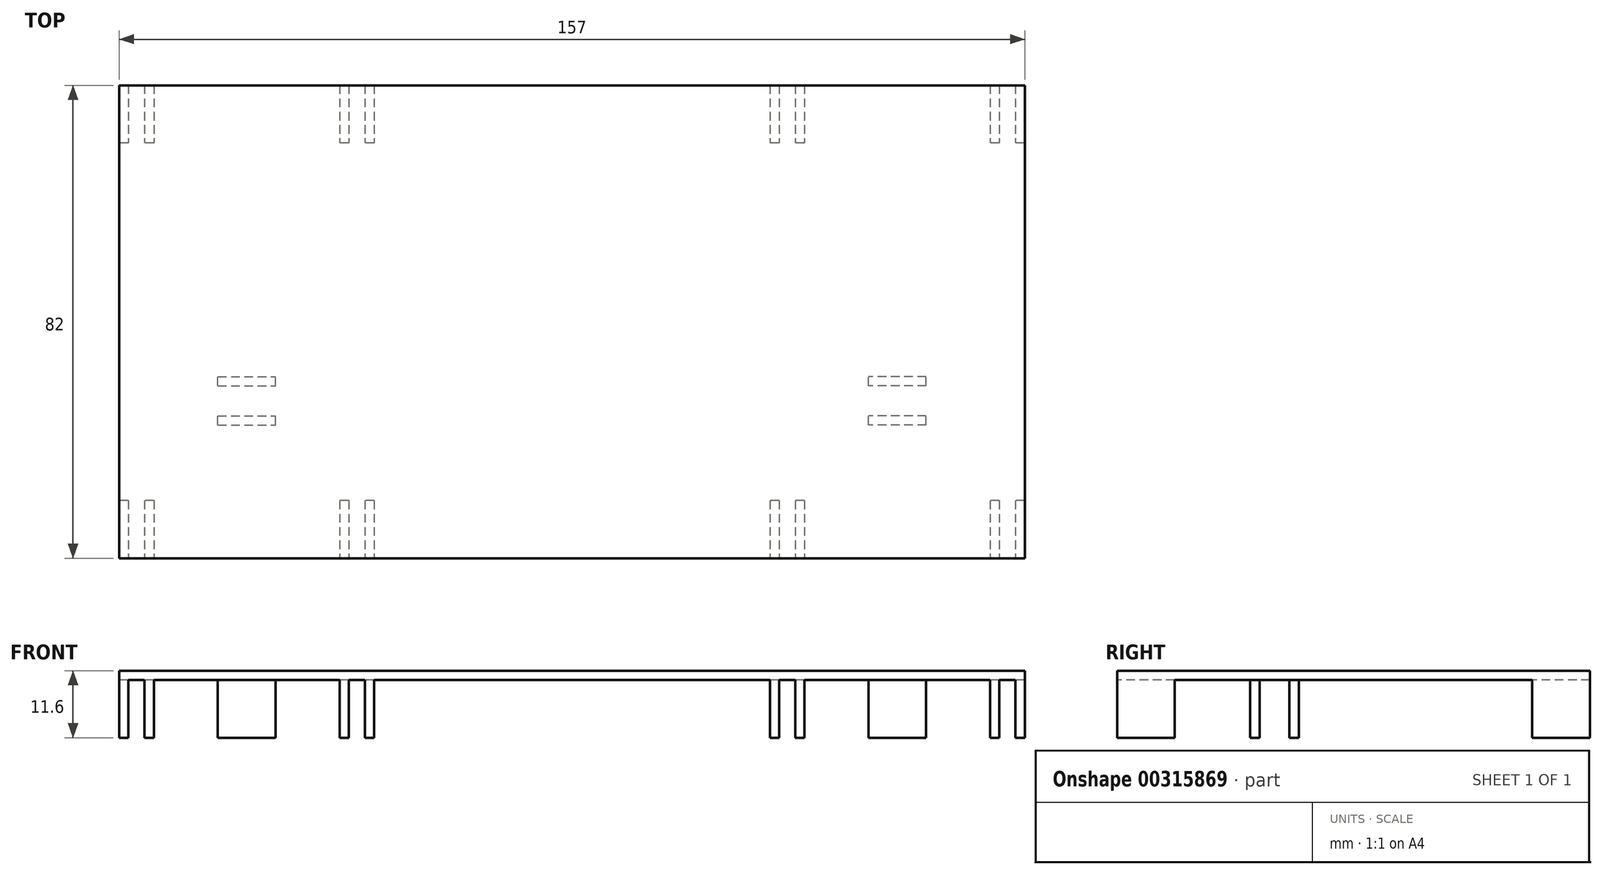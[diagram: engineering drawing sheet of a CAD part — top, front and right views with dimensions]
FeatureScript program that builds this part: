
annotation { "Feature Type Name" : "Feature", "Feature Type Description" : "" }
export const myFeature = defineFeature(function(context is Context, id is Id, definition is map)
    precondition{}
    {
        {
            var Q0;
            Q0=qCreatedBy(makeId("Front.planeOp"),FACE);
            cPlane(context, id + "F0", {"entities" : qUnion([Q0]), "cplaneType" : CPlaneType.OFFSET, "offset" : 41 * mm, "width" : 150 * mm, "height" : 150 * mm});
        }
        {
            var Q0;
            Q0=qCreatedBy(id+"F0.planeOp",FACE);
            var sketch = newSketch(context, id + "F1", { "sketchPlane" : qUnion([Q0])});
            skLineSegment(sketch, "E0", {"start": v(78.5, 1.6) * mm, "end": v(78.5, 0) * mm});
            skLineSegment(sketch, "E1", {"start": v(78.5, 0) * mm, "end": v(-78.5, 0) * mm});
            skLineSegment(sketch, "E2", {"start": v(-78.5, 0) * mm, "end": v(-78.5, 1.6) * mm});
            skLineSegment(sketch, "E3", {"start": v(-78.5, 1.6) * mm, "end": v(78.5, 1.6) * mm});
            skLineSegment(sketch, "E4", {"start": v(-78.5, 0) * mm, "end": v(-78.5, -10) * mm});
            skLineSegment(sketch, "E5", {"start": v(-78.5, -10) * mm, "end": v(-76.9, -10) * mm});
            skLineSegment(sketch, "E6", {"start": v(-76.9, -10) * mm, "end": v(-76.9, 0) * mm});
            skLineSegment(sketch, "E7", {"start": v(-78.5, 0) * mm, "end": v(-76.9, 0) * mm});
            skLineSegment(sketch, "E8", {"start": v(-74.1, 0) * mm, "end": v(-74.1, -10) * mm});
            skLineSegment(sketch, "E9", {"start": v(-74.1, -10) * mm, "end": v(-72.5, -10) * mm});
            skLineSegment(sketch, "E10", {"start": v(-72.5, -10) * mm, "end": v(-72.5, 0) * mm});
            skLineSegment(sketch, "E11", {"start": v(-72.5, 0) * mm, "end": v(-74.1, 0) * mm});
            skLineSegment(sketch, "E12", {"start": v(-35.9, 0) * mm, "end": v(-35.9, -10) * mm});
            skLineSegment(sketch, "E13", {"start": v(-35.9, -10) * mm, "end": v(-34.3, -10) * mm});
            skLineSegment(sketch, "E14", {"start": v(-34.3, -10) * mm, "end": v(-34.3, 0) * mm});
            skLineSegment(sketch, "E15", {"start": v(-34.3, 0) * mm, "end": v(-35.9, 0) * mm});
            skLineSegment(sketch, "E16", {"start": v(-38.7, 0) * mm, "end": v(-38.7, -10) * mm});
            skLineSegment(sketch, "E17", {"start": v(-38.7, -10) * mm, "end": v(-40.3, -10) * mm});
            skLineSegment(sketch, "E18", {"start": v(-40.3, -10) * mm, "end": v(-40.3, 0) * mm});
            skLineSegment(sketch, "E19", {"start": v(-40.3, 0) * mm, "end": v(-38.7, 0) * mm});
            skLineSegment(sketch, "E20.MirrorCS", {"start": v(34.3, -10) * mm, "end": v(34.3, 0) * mm});
            skLineSegment(sketch, "E21.MirrorCS", {"start": v(35.9, 0) * mm, "end": v(35.9, -10) * mm});
            skLineSegment(sketch, "E22.MirrorCS", {"start": v(40.3, -10) * mm, "end": v(40.3, 0) * mm});
            skLineSegment(sketch, "E23.MirrorCS", {"start": v(38.7, 0) * mm, "end": v(38.7, -10) * mm});
            skLineSegment(sketch, "E24.MirrorCS", {"start": v(38.7, -10) * mm, "end": v(40.3, -10) * mm});
            skLineSegment(sketch, "E25.MirrorCS", {"start": v(40.3, 0) * mm, "end": v(38.7, 0) * mm});
            skLineSegment(sketch, "E26.MirrorCS", {"start": v(74.1, 0) * mm, "end": v(74.1, -10) * mm});
            skLineSegment(sketch, "E27.MirrorCS", {"start": v(72.5, -10) * mm, "end": v(72.5, 0) * mm});
            skLineSegment(sketch, "E28.MirrorCS", {"start": v(72.5, 0) * mm, "end": v(74.1, 0) * mm});
            skLineSegment(sketch, "E29.MirrorCS", {"start": v(76.9, -10) * mm, "end": v(76.9, 0) * mm});
            skLineSegment(sketch, "E30.MirrorCS", {"start": v(78.5, 0) * mm, "end": v(76.9, 0) * mm});
            skLineSegment(sketch, "E31.MirrorCS", {"start": v(78.5, 0) * mm, "end": v(78.5, -10) * mm});
            skLineSegment(sketch, "E32.MirrorCS", {"start": v(78.5, -10) * mm, "end": v(76.9, -10) * mm});
            skLineSegment(sketch, "E33.MirrorCS", {"start": v(74.1, -10) * mm, "end": v(72.5, -10) * mm});
            skLineSegment(sketch, "E34.MirrorCS", {"start": v(35.9, -10) * mm, "end": v(34.3, -10) * mm});
            skLineSegment(sketch, "E35", {"start": v(-35.9, 0) * mm, "end": v(-34.3, 0) * mm});
            skLineSegment(sketch, "E36", {"start": v(34.3, 0) * mm, "end": v(35.9, 0) * mm});
            skSolve(sketch);
        }
        {
            var Q0;
            Q0=makeQuery(id+"F1.imprint","IMPRINT",FACE,{"disambiguationData":[TD([[makeQuery(id+"F1.imprint","IMPRINT",EDGE,{"derivedFrom":sQuery(id+"F1.wireOp",EDGE,"E0")}),-1.0]])]});
            extrude(context, id + "F2", {"entities" : qUnion([Q0]), "oppositeDirection" : true, "depth" : 82 * mm});
        }
        {
            var Q0;
            Q0=makeQuery(id+"F1.imprint","IMPRINT",FACE,{"disambiguationData":[TD([[makeQuery(id+"F1.imprint","IMPRINT",EDGE,{"derivedFrom":sQuery(id+"F1.wireOp",EDGE,"E4")}),1.0]])]});
            var Q1;
            Q1=makeQuery(id+"F1.imprint","IMPRINT",FACE,{"disambiguationData":[TD([[makeQuery(id+"F1.imprint","IMPRINT",EDGE,{"derivedFrom":sQuery(id+"F1.wireOp",EDGE,"E8")}),1.0]])]});
            var Q2;
            Q2=makeQuery(id+"F1.imprint","IMPRINT",FACE,{"disambiguationData":[TD([[makeQuery(id+"F1.imprint","IMPRINT",EDGE,{"derivedFrom":sQuery(id+"F1.wireOp",EDGE,"E16")}),-1.0]])]});
            var Q3;
            Q3=makeQuery(id+"F1.imprint","IMPRINT",FACE,{"disambiguationData":[TD([[makeQuery(id+"F1.imprint","IMPRINT",EDGE,{"derivedFrom":sQuery(id+"F1.wireOp",EDGE,"E12")}),1.0]])]});
            var Q4;
            Q4=makeQuery(id+"F1.imprint","IMPRINT",FACE,{"disambiguationData":[TD([[makeQuery(id+"F1.imprint","IMPRINT",EDGE,{"derivedFrom":sQuery(id+"F1.wireOp",EDGE,"E20.MirrorCS")}),-1.0]])]});
            var Q5;
            Q5=makeQuery(id+"F1.imprint","IMPRINT",FACE,{"disambiguationData":[TD([[makeQuery(id+"F1.imprint","IMPRINT",EDGE,{"derivedFrom":sQuery(id+"F1.wireOp",EDGE,"E22.MirrorCS")}),1.0]])]});
            var Q6;
            Q6=makeQuery(id+"F1.imprint","IMPRINT",FACE,{"disambiguationData":[TD([[makeQuery(id+"F1.imprint","IMPRINT",EDGE,{"derivedFrom":sQuery(id+"F1.wireOp",EDGE,"E26.MirrorCS")}),-1.0]])]});
            var Q7;
            Q7=makeQuery(id+"F1.imprint","IMPRINT",FACE,{"disambiguationData":[TD([[makeQuery(id+"F1.imprint","IMPRINT",EDGE,{"derivedFrom":sQuery(id+"F1.wireOp",EDGE,"E29.MirrorCS")}),-1.0]])]});
            extrude(context, id + "F3", {"entities" : qUnion([Q0, Q1, Q2, Q3, Q4, Q5, Q6, Q7]), "operationType" : NewBodyOperationType.ADD, "oppositeDirection" : true, "depth" : 10 * mm});
        }
        {
            var Q0;
            Q0=makeQuery(id+"F1.imprint","IMPRINT",FACE,{"disambiguationData":[TD([[makeQuery(id+"F1.imprint","IMPRINT",EDGE,{"derivedFrom":sQuery(id+"F1.wireOp",EDGE,"E4")}),1.0]])]});
            var Q1;
            Q1=makeQuery(id+"F1.imprint","IMPRINT",FACE,{"disambiguationData":[TD([[makeQuery(id+"F1.imprint","IMPRINT",EDGE,{"derivedFrom":sQuery(id+"F1.wireOp",EDGE,"E8")}),1.0]])]});
            var Q2;
            Q2=makeQuery(id+"F1.imprint","IMPRINT",FACE,{"disambiguationData":[TD([[makeQuery(id+"F1.imprint","IMPRINT",EDGE,{"derivedFrom":sQuery(id+"F1.wireOp",EDGE,"E16")}),-1.0]])]});
            var Q3;
            Q3=makeQuery(id+"F1.imprint","IMPRINT",FACE,{"disambiguationData":[TD([[makeQuery(id+"F1.imprint","IMPRINT",EDGE,{"derivedFrom":sQuery(id+"F1.wireOp",EDGE,"E12")}),1.0]])]});
            var Q4;
            Q4=makeQuery(id+"F1.imprint","IMPRINT",FACE,{"disambiguationData":[TD([[makeQuery(id+"F1.imprint","IMPRINT",EDGE,{"derivedFrom":sQuery(id+"F1.wireOp",EDGE,"E22.MirrorCS")}),1.0]])]});
            var Q5;
            Q5=makeQuery(id+"F1.imprint","IMPRINT",FACE,{"disambiguationData":[TD([[makeQuery(id+"F1.imprint","IMPRINT",EDGE,{"derivedFrom":sQuery(id+"F1.wireOp",EDGE,"E20.MirrorCS")}),-1.0]])]});
            var Q6;
            Q6=makeQuery(id+"F1.imprint","IMPRINT",FACE,{"disambiguationData":[TD([[makeQuery(id+"F1.imprint","IMPRINT",EDGE,{"derivedFrom":sQuery(id+"F1.wireOp",EDGE,"E26.MirrorCS")}),-1.0]])]});
            var Q7;
            Q7=makeQuery(id+"F1.imprint","IMPRINT",FACE,{"disambiguationData":[TD([[makeQuery(id+"F1.imprint","IMPRINT",EDGE,{"derivedFrom":sQuery(id+"F1.wireOp",EDGE,"E29.MirrorCS")}),-1.0]])]});
            extrude(context, id + "F4", {"entities" : qUnion([Q0, Q1, Q2, Q3, Q4, Q5, Q6, Q7]), "operationType" : NewBodyOperationType.ADD, "oppositeDirection" : true, "depth" : 82 * mm, "hasSecondDirection" : true, "secondDirectionOppositeDirection" : true, "secondDirectionDepth" : 72 * mm});
        }
        {
            var Q0;
            Q0=qCreatedBy(makeId("Right.planeOp"),FACE);
            cPlane(context, id + "F5", {"entities" : qUnion([Q0]), "cplaneType" : CPlaneType.OFFSET, "offset" : 51.4 * mm, "oppositeDirection" : true, "width" : 150 * mm, "height" : 150 * mm});
        }
        {
            var Q0;
            Q0=qCreatedBy(id+"F5.planeOp",FACE);
            var sketch = newSketch(context, id + "F6", { "sketchPlane" : qUnion([Q0])});
            skLineSegment(sketch, "E37", {"start": v(-9.5, 0) * mm, "end": v(-9.5, -10) * mm});
            skLineSegment(sketch, "E38", {"start": v(-9.5, -10) * mm, "end": v(-11.1, -10) * mm});
            skLineSegment(sketch, "E39", {"start": v(-11.1, -10) * mm, "end": v(-11.1, 0) * mm});
            skLineSegment(sketch, "E40", {"start": v(-11.1, 0) * mm, "end": v(-9.5, 0) * mm});
            skLineSegment(sketch, "E41", {"start": v(-16.3, 0) * mm, "end": v(-16.3, -10) * mm});
            skLineSegment(sketch, "E42", {"start": v(-16.3, -10) * mm, "end": v(-17.9, -10) * mm});
            skLineSegment(sketch, "E43", {"start": v(-17.9, -10) * mm, "end": v(-17.9, 0) * mm});
            skLineSegment(sketch, "E44", {"start": v(-17.9, 0) * mm, "end": v(-16.3, 0) * mm});
            skSolve(sketch);
        }
        {
            var Q0;
            Q0 = qSketchRegion(id + "F6", true);
            extrude(context, id + "F7", {"entities" : qUnion([Q0]), "operationType" : NewBodyOperationType.ADD, "oppositeDirection" : true, "depth" : 10 * mm});
        }
        {
            var Q0;
            Q0 = qSketchRegion(id + "F6", true);
            extrude(context, id + "F8", {"entities" : qUnion([Q0]), "operationType" : NewBodyOperationType.ADD, "depth" : 112.8 * mm, "hasSecondDirection" : true, "secondDirectionOppositeDirection" : false, "secondDirectionDepth" : 102.8 * mm});
        }
    });
